# Revit family: Lüftungsrohrschelle Doppio, M 8-M10, DN 71-200, Gummi
name_source: partatom
category: HLS-Bauteile
revit_build: Autodesk Revit 2017 (Build: 20190507_1515(x64)
units: mm (PartAtom-declared; Revit-internal decimal feet)

## family parameters
Arbeitsebenenbasiert = Ja
Beim Laden mit Abzugskörper schneiden = Nein
Bemaßung runder Anschluss = Durchmesser verwenden
Gemeinsam genutzt = Ja
Immer vertikal = Nein
Raumberechnungspunkt = Nein
Teiletyp = Normal

## types (11) — shared parameters
A = 24 mm  [stored 0.0787402 ft]
Anschluss = M8/M10
Anschlußhöhe = 24 mm
Bauart = zweiteilig
Baustoffklasse = B2
DF1 = 23 mm  [stored 0.0754593 ft]
DF2 = 36 mm  [stored 0.11811 ft]
DS = 5 mm  [stored 0.0164042 ft]
DVS = 6 mm  [stored 0.019685 ft]
Dämmstärke = 5 mm  [stored 0.0164042 ft]
Fabrikat = MEFA
Farbe Schalldämmeinlage = schwarz
Firma = MEFA Befestigungs- und Montagesysteme GmbH
Gesamthöhe Dämmung = 8 mm  [stored 0.0262467 ft]
HGA = 17 mm  [stored 0.0557743 ft]
Kurztext1 = Lüftungsschelle Doppio 20x1,5
MB = 20 mm  [stored 0.0656168 ft]
MD = 2 mm  [stored 0.00656168 ft]
Material = Stahl
Material Schalldämmeinlage = TPE
Materialmaße = 20x1,5 mm
Materialname = S235
Mengeneinheit = St
Oberflaeche = galvanisch verzinkt
Rohraußendurchmesser Zoll = Zoll
Schalldämmeinlage = Gummi
Sicke = 1 mm  [stored 0.00328084 ft]
Verschluss = mit Rastverschluss
Verschluss-Schraube = M6
Vorgabe-Ansicht = 1219 mm
max. Temperaturbeständigkeit = 100 °C
max. zul. Last = 0.61 kN
max. zul. Last horizontal = 0.00 kN
max. zul. Last vertikal = 0.00 kN
zero-valued in all types: AB, L1, Stärke Material, max. Rohraußendurchmesser, min. Rohraußendurchmesser

## per-type parameters (varying)
| type | Artikelnummer | B | Breite | D | D0 | DN | EAN | Gewicht | Gewicht pro Bauteil | H | Höhe | Kurztext2 | Nennweite DN Rohr | R | RM | Rohraußendurchmesser | S | max. Höhe | vpe |
| Lüftungsrohrschelle Doppio, M8/M10, DN  71, Gummi | 0449071 | 107 mm | 107 mm | 72 mm  [stored 0.23622 ft] | 81 mm  [stored 0.265748 ft] | 71 mm  [stored 0.23294 ft] | 4250928410900 | 0.13 kg | 0.13 kg | 104 mm | 104 mm | DN 71 M8/M10 TPE | 71 mm  [stored 0.23294 ft] | 41 mm | 42 mm | 73 mm  [stored 0.239501 ft] | 95 mm  [stored 0.31168 ft] | 104 mm | 50 St |
| Lüftungsrohrschelle Doppio, M8/M10, DN  80, Gummi | 0449080 | 116 mm | 116 mm | 81 mm  [stored 0.265748 ft] | 90 mm  [stored 0.295276 ft] | 80 mm  [stored 0.262467 ft] | 4250928410917 | 0.01 kg | 0.01 kg | 113 mm | 113 mm | DN 80 M8/M10 TPE | 80 mm  [stored 0.262467 ft] | 45 mm  [stored 0.147638 ft] | 47 mm | 82 mm  [stored 0.269029 ft] | 104 mm | 113 mm | 50 St |
| Lüftungsrohrschelle Doppio, M8/M10, DN  90, Gummi | 0449090 | 127 mm | 126 mm | 91 mm  [stored 0.298556 ft] | 100 mm  [stored 0.328084 ft] | 91 mm  [stored 0.298556 ft] | 4250928410924 | 0.15 kg | 0.15 kg | 123 mm | 123 mm | DN 90 M8/M10 TPE | 90 mm  [stored 0.295276 ft] | 50 mm  [stored 0.164042 ft] | 52 mm | 92 mm  [stored 0.301837 ft] | 114 mm | 123 mm | 50 St |
| Lüftungsrohrschelle Doppio, M8/M10, DN 100, Gummi | 0449100 | 136 mm | 136 mm | 102 mm | 111 mm | 100 mm  [stored 0.328084 ft] | 4250928410931 | 0.16 kg | 0.16 kg | 134 mm | 134 mm | DN 100 M8/M10 TPE | 100 mm  [stored 0.328084 ft] | 56 mm | 57 mm  [stored 0.187008 ft] | 103 mm | 125 mm | 134 mm | 50 St |
| Lüftungsrohrschelle Doppio, M8/M10, DN 112, Gummi | 0449112 | 148 mm | 148 mm | 114 mm | 123 mm | 112 mm | 4250928410948 | 0.17 kg | 0.17 kg | 146 mm | 146 mm | DN 112 M8/M10 TPE | 112 mm | 62 mm | 63 mm  [stored 0.206693 ft] | 115 mm | 137 mm | 146 mm | 50 St |
| Lüftungsrohrschelle Doppio, M8/M10, DN 125, Gummi | 0449125 | 161 mm | 161 mm | 128 mm | 137 mm | 125 mm | 4250928410955 | 0.19 kg | 0.19 kg | 160 mm | 159 mm | DN 125 M8/M10 TPE | 125 mm | 69 mm  [stored 0.226378 ft] | 70 mm  [stored 0.229659 ft] | 128 mm | 151 mm | 159 mm | 50 St |
| Lüftungsrohrschelle Doppio, M8/M10, DN 140, Gummi | 0449140 | 176 mm | 176 mm | 142 mm | 151 mm | 140 mm | 4250928410962 | 0.20 kg | 0.20 kg | 174 mm | 174 mm | DN 140 M8/M10 TPE | 140 mm | 76 mm | 77 mm  [stored 0.252625 ft] | 143 mm | 165 mm | 174 mm | 25 St |
| Lüftungsrohrschelle Doppio, M8/M10, DN 150, Gummi | 0449150 | 186 mm | 186 mm | 152 mm | 161 mm | 150 mm | 4250928410979 | 0.22 kg | 0.22 kg | 184 mm | 184 mm | DN 150 M8/M10 TPE | 150 mm | 81 mm  [stored 0.265748 ft] | 82 mm  [stored 0.269029 ft] | 153 mm | 175 mm | 184 mm | 25 St |
| Lüftungsrohrschelle Doppio, M8/M10, DN 160, Gummi | 0449160 | 196 mm | 196 mm | 162 mm | 171 mm | 160 mm | 4250928410986 | 0.23 kg | 0.23 kg | 194 mm | 194 mm | DN 160 M8/M10 TPE | 160 mm | 86 mm | 87 mm | 163 mm | 185 mm | 194 mm | 25 St |
| Lüftungsrohrschelle Doppio, M8/M10, DN 180, Gummi | 0449160 | 216 mm | 196 mm | 182 mm | 191 mm | 180 mm | 4250928410986 | 0.23 kg | 0.23 kg | 214 mm | 194 mm | DN 160 M8/M10 TPE | 160 mm | 96 mm | 97 mm  [stored 0.318241 ft] | 163 mm | 205 mm | 194 mm | 25 St |
| Lüftungsrohrschelle Doppio, M8/M10, DN 200, Gummi | 0449200 | 236 mm | 236 mm | 202 mm | 211 mm | 200 mm | 4250928411006 | 0.27 kg | 0.27 kg | 234 mm | 234 mm | DN 200 M8/M10 TPE | 200 mm | 106 mm | 107 mm | 203 mm | 225 mm | 234 mm | 25 St |

note: [stored X ft] marks values corroborated as IEEE doubles in the binary element streams (Revit-internal decimal feet)

## geometry (parser evidence)
native form markers: Sweep x6
no freeform markers — native parametric forms only
